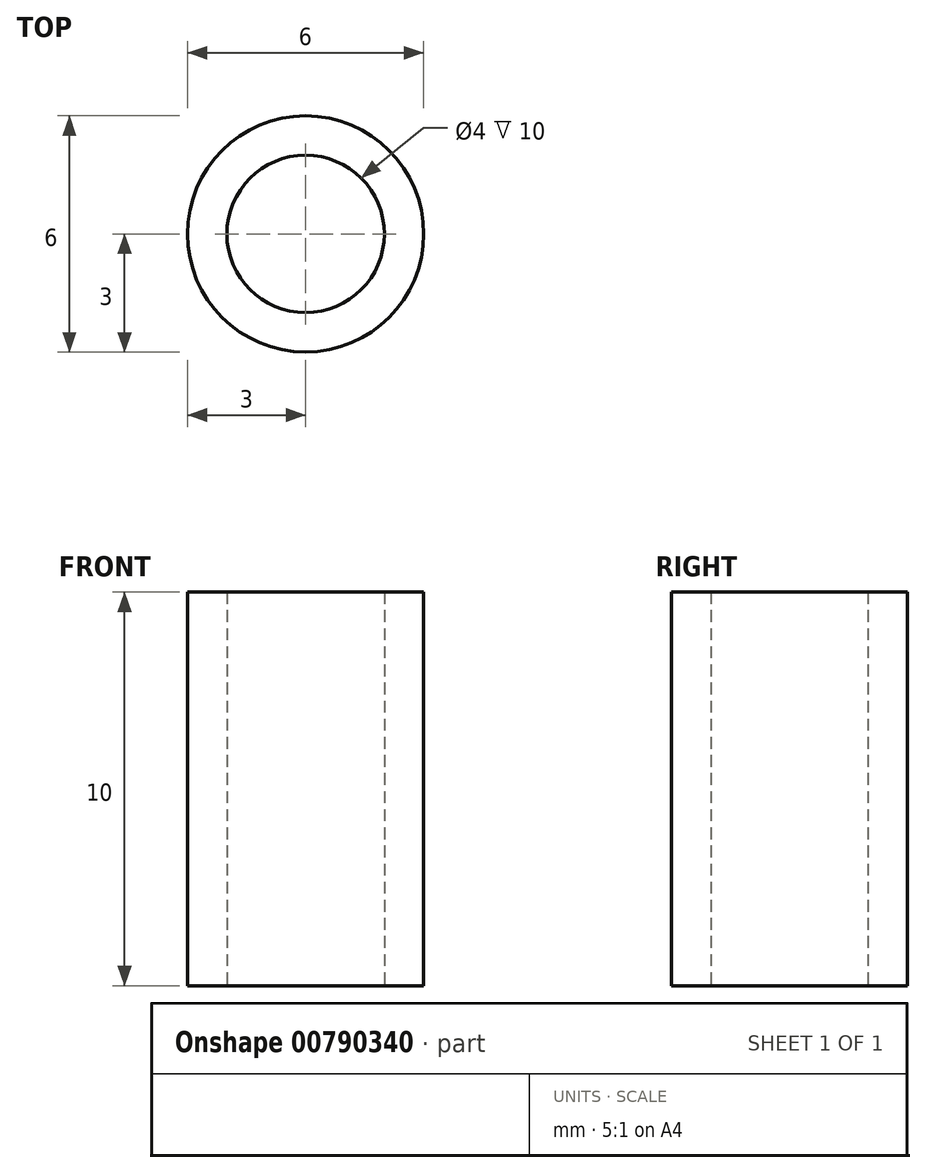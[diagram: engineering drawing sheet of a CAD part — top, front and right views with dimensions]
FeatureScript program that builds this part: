
annotation { "Feature Type Name" : "Feature", "Feature Type Description" : "" }
export const myFeature = defineFeature(function(context is Context, id is Id, definition is map)
    precondition{}
    {
        {
            var Q0;
            Q0=qCreatedBy(makeId("Top.planeOp"),FACE);
            var sketch = newSketch(context, id + "F0", { "sketchPlane" : qUnion([Q0])});
            skCircle(sketch, "E0", {"center": v(0, 0) * mm, "radius": 2 * mm});
            skCircle(sketch, "E1", {"center": v(0, 0) * mm, "radius": 3 * mm});
            skSolve(sketch);
        }
        {
            var Q0;
            Q0=makeQuery(id+"F0.imprint","IMPRINT",FACE,{"disambiguationData":[TD([[makeQuery(id+"F0.imprint","IMPRINT",EDGE,{"derivedFrom":sQuery(id+"F0.wireOp",EDGE,"E0")}),-1.0]])]});
            extrude(context, id + "F1", {"entities" : qUnion([Q0]), "depth" : 10 * mm, "offsetDistance" : 25 * mm});
        }
    });
